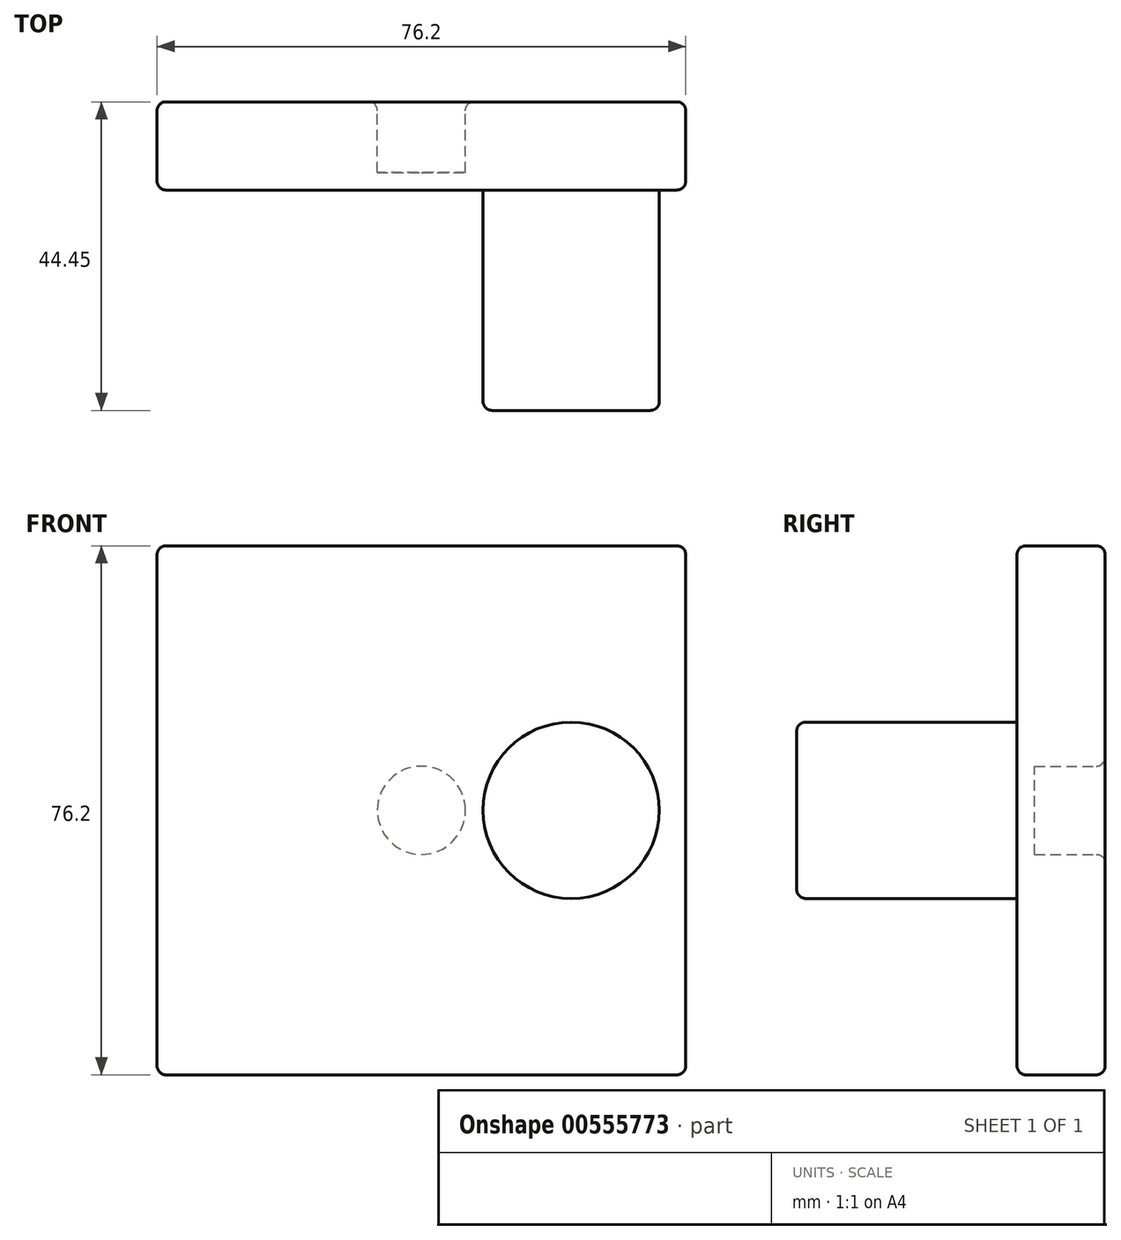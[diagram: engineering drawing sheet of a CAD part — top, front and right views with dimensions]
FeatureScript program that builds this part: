
annotation { "Feature Type Name" : "Feature", "Feature Type Description" : "" }
export const myFeature = defineFeature(function(context is Context, id is Id, definition is map)
    precondition{}
    {
        {
            var Q0;
            Q0=qCreatedBy(makeId("Front.planeOp"),FACE);
            var sketch = newSketch(context, id + "F0", { "sketchPlane" : qUnion([Q0])});
            skLineSegment(sketch, "E0.bottom", {"start": v(38.1, 38.1) * mm, "end": v(-38.1, 38.1) * mm});
            skLineSegment(sketch, "E0.top", {"start": v(38.1, -38.1) * mm, "end": v(-38.1, -38.1) * mm});
            skLineSegment(sketch, "E0.left", {"start": v(38.1, 38.1) * mm, "end": v(38.1, -38.1) * mm});
            skLineSegment(sketch, "E0.right", {"start": v(-38.1, 38.1) * mm, "end": v(-38.1, -38.1) * mm});
            skPoint(sketch, "E0.middle", {"position": v(0, 0) * mm});
            skCircle(sketch, "E1", {"center": v(0, 0) * mm, "radius": 6.35 * mm});
            skSolve(sketch);
        }
        {
            var Q0;
            Q0=makeQuery(id+"F0.imprint","IMPRINT",FACE,{"disambiguationData":[TD([[makeQuery(id+"F0.imprint","IMPRINT",EDGE,{"derivedFrom":sQuery(id+"F0.wireOp",EDGE,"E0.bottom")}),1.0]])]});
            extrude(context, id + "F1", {"entities" : qUnion([Q0]), "depth" : 12.7 * mm, "offsetDistance" : 25.4 * mm});
        }
        {
            var Q0;
            Q0=makeQuery(id+"F1.opExtrude","CAP_FACE",FACE,{"disambiguationData":[OSD([sQuery(id+"F0.wireOp",EDGE,"E0.bottom"),sQuery(id+"F0.wireOp",EDGE,"E0.top"),sQuery(id+"F0.wireOp",EDGE,"E0.left"),sQuery(id+"F0.wireOp",EDGE,"E0.right")])],"isStart":false});
            var sketch = newSketch(context, id + "F2", { "sketchPlane" : qUnion([Q0])});
            skCircle(sketch, "E2", {"center": v(21.59, 0) * mm, "radius": 12.7 * mm});
            skSolve(sketch);
        }
        {
            var Q0;
            Q0=makeQuery(id+"F2.imprint","IMPRINT",FACE,{"disambiguationData":[TD([[makeQuery(id+"F2.imprint","IMPRINT",EDGE,{"derivedFrom":sQuery(id+"F2.wireOp",EDGE,"E2")}),1.0]])]});
            extrude(context, id + "F3", {"entities" : qUnion([Q0]), "operationType" : NewBodyOperationType.ADD, "depth" : 31.75 * mm, "offsetDistance" : 25.4 * mm});
        }
        {
            var Q0;
            Q0=makeQuery(id+"F1.opExtrude","CAP_FACE",FACE,{"disambiguationData":[OSD([sQuery(id+"F0.wireOp",EDGE,"E0.bottom"),sQuery(id+"F0.wireOp",EDGE,"E0.top"),sQuery(id+"F0.wireOp",EDGE,"E0.left"),sQuery(id+"F0.wireOp",EDGE,"E0.right")])],"isStart":true});
            var Q1;
            Q1=makeQuery(id+"F1.opExtrude","SWEPT_FACE",FACE,{"disambiguationData":[OSD([sQuery(id+"F0.wireOp",EDGE,"E0.left")])]});
            var Q2;
            Q2=makeQuery(id+"F1.opExtrude","SWEPT_EDGE",EDGE,{"disambiguationData":[OSD([sQuery(id+"F0.wireOp",EDGE,"E0.top"),sQuery(id+"F0.wireOp",EDGE,"E0.right")])]});
            var Q3;
            Q3=makeQuery(id+"F1.opExtrude","SWEPT_EDGE",EDGE,{"disambiguationData":[OSD([sQuery(id+"F0.wireOp",EDGE,"E0.bottom"),sQuery(id+"F0.wireOp",EDGE,"E0.right")])]});
            var Q4;
            Q4=makeQuery(id+"F3.opExtrude","CAP_EDGE",EDGE,{"disambiguationData":[OSD([sQuery(id+"F2.wireOp",EDGE,"E2")])],"isStart":false});
            var Q5;
            Q5=makeQuery(id+"F1.opExtrude","CAP_EDGE",EDGE,{"disambiguationData":[OSD([sQuery(id+"F0.wireOp",EDGE,"E0.top")])],"isStart":false});
            var Q6;
            Q6=makeQuery(id+"F1.opExtrude","CAP_EDGE",EDGE,{"disambiguationData":[OSD([sQuery(id+"F0.wireOp",EDGE,"E0.right")])],"isStart":false});
            var Q7;
            Q7=makeQuery(id+"F1.opExtrude","CAP_EDGE",EDGE,{"disambiguationData":[OSD([sQuery(id+"F0.wireOp",EDGE,"E0.bottom")])],"isStart":false});
            fillet(context, id + "F4", {"entities" : qUnion([Q0, Q1, Q2, Q3, Q4, Q5, Q6, Q7]), "radius" : 1.27 * mm, "tangentPropagation" : true, "allowEdgeOverflow" : false});
        }
        {
            var Q0;
            Q0=makeQuery(id+"F1.opExtrude","CAP_FACE",FACE,{"disambiguationData":[OSD([sQuery(id+"F0.wireOp",EDGE,"E0.bottom"),sQuery(id+"F0.wireOp",EDGE,"E0.top"),sQuery(id+"F0.wireOp",EDGE,"E0.left"),sQuery(id+"F0.wireOp",EDGE,"E0.right"),sQuery(id+"F0.wireOp",EDGE,"E1")])],"isStart":false});
            var sketch = newSketch(context, id + "F5", { "sketchPlane" : qUnion([Q0])});
            skCircle(sketch, "E3", {"center": v(0, 0) * mm, "radius": 6.35 * mm});
            skSolve(sketch);
        }
        {
            var Q0;
            Q0=makeQuery(id+"F5.imprint","IMPRINT",FACE,{"disambiguationData":[TD([[makeQuery(id+"F5.imprint","IMPRINT",EDGE,{"derivedFrom":sQuery(id+"F5.wireOp",EDGE,"E3")}),1.0]])]});
            extrude(context, id + "F6", {"entities" : qUnion([Q0]), "operationType" : NewBodyOperationType.ADD, "oppositeDirection" : true, "depth" : 2.54 * mm, "offsetDistance" : 25.4 * mm});
        }
    });
